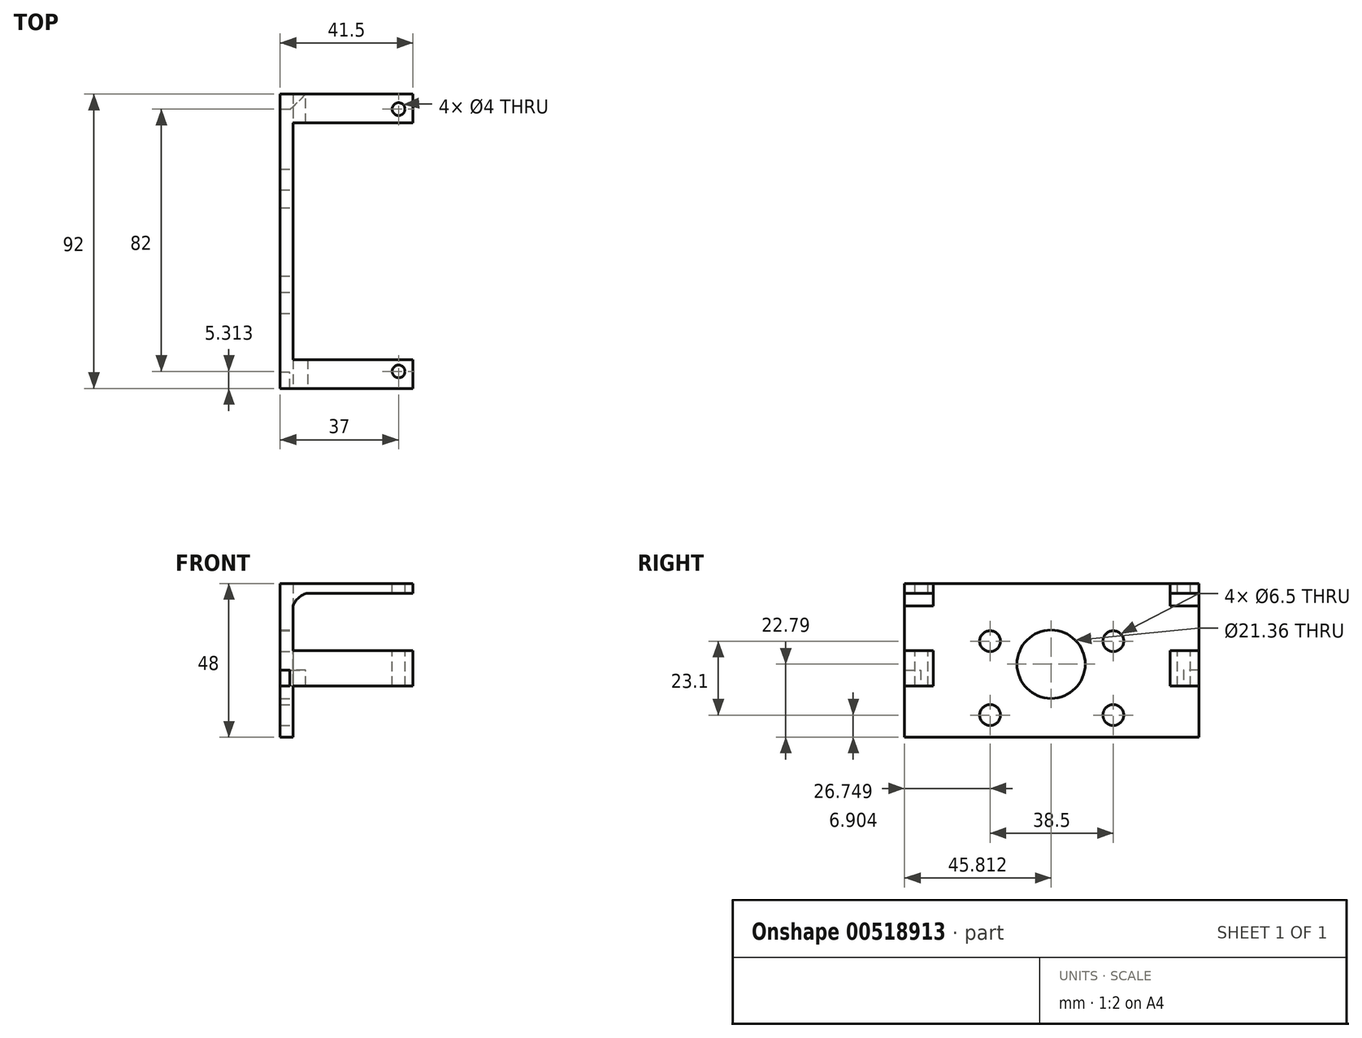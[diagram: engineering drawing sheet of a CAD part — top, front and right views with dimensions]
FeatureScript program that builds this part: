
annotation { "Feature Type Name" : "Feature", "Feature Type Description" : "" }
export const myFeature = defineFeature(function(context is Context, id is Id, definition is map)
    precondition{}
    {
        {
            var Q0;
            Q0=qCreatedBy(makeId("Right.planeOp"),FACE);
            var sketch = newSketch(context, id + "F0", { "sketchPlane" : qUnion([Q0])});
            skLineSegment(sketch, "E0.bottom", {"start": v(-93.03, 7.83) * mm, "end": v(-1.03, 7.83) * mm});
            skLineSegment(sketch, "E0.top", {"start": v(-93.03, -40.17) * mm, "end": v(-1.03, -40.17) * mm});
            skLineSegment(sketch, "E0.left", {"start": v(-93.03, 7.83) * mm, "end": v(-93.03, -40.17) * mm});
            skLineSegment(sketch, "E0.right", {"start": v(-1.03, 7.83) * mm, "end": v(-1.03, -40.17) * mm});
            skSolve(sketch);
        }
        {
            var Q0;
            Q0 = qSketchRegion(id + "F0", true);
            extrude(context, id + "F1", {"entities" : qUnion([Q0]), "depth" : 4 * mm, "offsetDistance" : 25 * mm});
        }
        {
            var Q0;
            Q0=makeQuery(id+"F1.opExtrude","CAP_FACE",FACE,{"disambiguationData":[OSD([sQuery(id+"F0.wireOp",EDGE,"E0.bottom"),sQuery(id+"F0.wireOp",EDGE,"E0.top"),sQuery(id+"F0.wireOp",EDGE,"E0.left"),sQuery(id+"F0.wireOp",EDGE,"E0.right")])],"isStart":false});
            var sketch = newSketch(context, id + "F2", { "sketchPlane" : qUnion([Q0])});
            skCircle(sketch, "E1", {"center": v(-66.28, -10.17) * mm, "radius": 3.25 * mm});
            skCircle(sketch, "E2", {"center": v(-27.78, -10.17) * mm, "radius": 3.25 * mm});
            skCircle(sketch, "E3", {"center": v(-66.28, -33.27) * mm, "radius": 3.25 * mm});
            skCircle(sketch, "E4", {"center": v(-27.78, -33.27) * mm, "radius": 3.25 * mm});
            skLineSegment(sketch, "E5", {"start": v(-27.78, -10.17) * mm, "end": v(-1.03, -10.17) * mm, "construction": true});
            skLineSegment(sketch, "E6", {"start": v(-66.28, -10.17) * mm, "end": v(-93.03, -10.17) * mm, "construction": true});
            skCircle(sketch, "E7", {"center": v(-47.22, -17.38) * mm, "radius": 10.68 * mm});
            skSolve(sketch);
        }
        {
            var Q0;
            Q0 = qSketchRegion(id + "F2", true);
            extrude(context, id + "F3", {"entities" : qUnion([Q0]), "operationType" : NewBodyOperationType.REMOVE, "oppositeDirection" : true, "depth" : 25 * mm, "offsetDistance" : 25 * mm});
        }
        {
            var Q0;
            Q0=makeQuery(id+"F1.opExtrude","CAP_FACE",FACE,{"disambiguationData":[OSD([sQuery(id+"F0.wireOp",EDGE,"E0.bottom"),sQuery(id+"F0.wireOp",EDGE,"E0.top"),sQuery(id+"F0.wireOp",EDGE,"E0.left"),sQuery(id+"F0.wireOp",EDGE,"E0.right")])],"isStart":false});
            var sketch = newSketch(context, id + "F4", { "sketchPlane" : qUnion([Q0])});
            skLineSegment(sketch, "E8.bottom", {"start": v(-93.03, -13.17) * mm, "end": v(-84.03, -13.17) * mm});
            skLineSegment(sketch, "E8.top", {"start": v(-93.03, -24.17) * mm, "end": v(-84.03, -24.17) * mm});
            skLineSegment(sketch, "E8.left", {"start": v(-93.03, -13.17) * mm, "end": v(-93.03, -24.17) * mm});
            skLineSegment(sketch, "E8.right", {"start": v(-84.03, -13.17) * mm, "end": v(-84.03, -24.17) * mm});
            skLineSegment(sketch, "E9.bottom", {"start": v(-1.03, -13.17) * mm, "end": v(-10.03, -13.17) * mm});
            skLineSegment(sketch, "E9.top", {"start": v(-1.03, -24.17) * mm, "end": v(-10.03, -24.17) * mm});
            skLineSegment(sketch, "E9.left", {"start": v(-1.03, -13.17) * mm, "end": v(-1.03, -24.17) * mm});
            skLineSegment(sketch, "E9.right", {"start": v(-10.03, -13.17) * mm, "end": v(-10.03, -24.17) * mm});
            skLineSegment(sketch, "E10.bottom", {"start": v(-93.03, 7.83) * mm, "end": v(-84.03, 7.83) * mm});
            skLineSegment(sketch, "E10.top", {"start": v(-93.03, 4.83) * mm, "end": v(-84.03, 4.83) * mm});
            skLineSegment(sketch, "E10.left", {"start": v(-93.03, 7.83) * mm, "end": v(-93.03, 4.83) * mm});
            skLineSegment(sketch, "E10.right", {"start": v(-84.03, 7.83) * mm, "end": v(-84.03, 4.83) * mm});
            skLineSegment(sketch, "E11.bottom", {"start": v(-1.03, 7.83) * mm, "end": v(-10.03, 7.83) * mm});
            skLineSegment(sketch, "E11.top", {"start": v(-1.03, 4.83) * mm, "end": v(-10.03, 4.83) * mm});
            skLineSegment(sketch, "E11.left", {"start": v(-1.03, 7.83) * mm, "end": v(-1.03, 4.83) * mm});
            skLineSegment(sketch, "E11.right", {"start": v(-10.03, 7.83) * mm, "end": v(-10.03, 4.83) * mm});
            skSolve(sketch);
        }
        {
            var Q0;
            Q0=makeQuery(id+"F4.imprint","IMPRINT",FACE,{"disambiguationData":[TD([[makeQuery(id+"F4.imprint","IMPRINT",EDGE,{"derivedFrom":sQuery(id+"F4.wireOp",EDGE,"E8.bottom")}),-1.0]])]});
            var Q1;
            Q1=makeQuery(id+"F4.imprint","IMPRINT",FACE,{"disambiguationData":[TD([[makeQuery(id+"F4.imprint","IMPRINT",EDGE,{"derivedFrom":sQuery(id+"F4.wireOp",EDGE,"E9.bottom")}),1.0]])]});
            var Q2;
            Q2=makeQuery(id+"F4.imprint","IMPRINT",FACE,{"disambiguationData":[TD([[makeQuery(id+"F4.imprint","IMPRINT",EDGE,{"derivedFrom":sQuery(id+"F4.wireOp",EDGE,"E10.bottom")}),-1.0]])]});
            var Q3;
            Q3=makeQuery(id+"F4.imprint","IMPRINT",FACE,{"disambiguationData":[TD([[makeQuery(id+"F4.imprint","IMPRINT",EDGE,{"derivedFrom":sQuery(id+"F4.wireOp",EDGE,"E11.bottom")}),-1.0]])]});
            extrude(context, id + "F5", {"entities" : qUnion([Q0, Q1, Q2, Q3]), "operationType" : NewBodyOperationType.ADD, "depth" : 37.5 * mm, "offsetDistance" : 25 * mm});
        }
        {
            var Q0;
            Q0=makeQuery(id+"F5.boolean.opBoolean","MERGE",FACE,{"derivedFrom":[makeQuery(id+"F1.opExtrude","SWEPT_FACE",FACE,{"disambiguationData":[OSD([sQuery(id+"F0.wireOp",EDGE,"E0.bottom")])]}),makeQuery(id+"F5.opExtrude","SWEPT_FACE",FACE,{"disambiguationData":[OSD([sQuery(id+"F4.wireOp",EDGE,"E10.bottom")])]}),makeQuery(id+"F5.opExtrude","SWEPT_FACE",FACE,{"disambiguationData":[OSD([sQuery(id+"F4.wireOp",EDGE,"E11.bottom")])]})]});
            var sketch = newSketch(context, id + "F6", { "sketchPlane" : qUnion([Q0])});
            skCircle(sketch, "E12", {"center": v(37, -5.72) * mm, "radius": 2 * mm});
            skCircle(sketch, "E13", {"center": v(37, -87.72) * mm, "radius": 2 * mm});
            skSolve(sketch);
        }
        {
            var Q0;
            Q0 = qSketchRegion(id + "F6", true);
            extrude(context, id + "F7", {"entities" : qUnion([Q0]), "operationType" : NewBodyOperationType.REMOVE, "oppositeDirection" : true, "depth" : 40 * mm, "offsetDistance" : 25 * mm});
        }
        {
            var Q0;
            Q0=makeQuery(id+"F1.opExtrude","CAP_FACE",FACE,{"disambiguationData":[OSD([sQuery(id+"F0.wireOp",EDGE,"E0.bottom"),sQuery(id+"F0.wireOp",EDGE,"E0.top"),sQuery(id+"F0.wireOp",EDGE,"E0.left"),sQuery(id+"F0.wireOp",EDGE,"E0.right")])],"isStart":true});
            var sketch = newSketch(context, id + "F8", { "sketchPlane" : qUnion([Q0])});
            skLineSegment(sketch, "E14.bottom", {"start": v(0.85, -19.22) * mm, "end": v(5.85, -19.22) * mm});
            skLineSegment(sketch, "E14.top", {"start": v(0.85, -24.22) * mm, "end": v(5.85, -24.22) * mm});
            skLineSegment(sketch, "E14.left", {"start": v(0.85, -19.22) * mm, "end": v(0.85, -24.22) * mm});
            skLineSegment(sketch, "E14.right", {"start": v(5.85, -19.22) * mm, "end": v(5.85, -24.22) * mm});
            skLineSegment(sketch, "E15.bottom", {"start": v(93.03, -19.22) * mm, "end": v(88.03, -19.22) * mm});
            skLineSegment(sketch, "E15.top", {"start": v(93.03, -24.22) * mm, "end": v(88.03, -24.22) * mm});
            skLineSegment(sketch, "E15.left", {"start": v(93.03, -19.22) * mm, "end": v(93.03, -24.22) * mm});
            skLineSegment(sketch, "E15.right", {"start": v(88.03, -19.22) * mm, "end": v(88.03, -24.22) * mm});
            skLineSegment(sketch, "E16", {"start": v(27.78, -10.17) * mm, "end": v(5.85, -19.22) * mm, "construction": true});
            skLineSegment(sketch, "E17", {"start": v(5.85, -24.22) * mm, "end": v(27.78, -33.27) * mm, "construction": true});
            skSolve(sketch);
        }
        {
            var Q0;
            Q0=makeQuery(id+"F8.imprint","IMPRINT",FACE,{"disambiguationData":[TD([[makeQuery(id+"F8.imprint","IMPRINT",EDGE,{"derivedFrom":sQuery(id+"F8.wireOp",EDGE,"E14.bottom")}),-1.0]])]});
            var Q1;
            Q1=makeQuery(id+"F8.imprint","IMPRINT",FACE,{"disambiguationData":[TD([[makeQuery(id+"F8.imprint","IMPRINT",EDGE,{"derivedFrom":sQuery(id+"F8.wireOp",EDGE,"E15.bottom")}),1.0]])]});
            extrude(context, id + "F9", {"entities" : qUnion([Q0, Q1]), "operationType" : NewBodyOperationType.REMOVE, "oppositeDirection" : true, "depth" : 3 * mm, "offsetDistance" : 25 * mm});
        }
        {
            var Q0;
            Q0=makeQuery(id+"F9.boolean.opBoolean","INTERSECT",EDGE,{"derivedFrom":[makeQuery(id+"F5.boolean.opBoolean","MERGE",FACE,{"derivedFrom":[makeQuery(id+"F1.opExtrude","SWEPT_FACE",FACE,{"disambiguationData":[OSD([sQuery(id+"F0.wireOp",EDGE,"E0.right")])]}),makeQuery(id+"F5.opExtrude","SWEPT_FACE",FACE,{"disambiguationData":[OSD([sQuery(id+"F4.wireOp",EDGE,"E9.left")])]}),makeQuery(id+"F5.opExtrude","SWEPT_FACE",FACE,{"disambiguationData":[OSD([sQuery(id+"F4.wireOp",EDGE,"E11.left")])]})]}),makeQuery(id+"F9.opExtrude","CAP_FACE",FACE,{"disambiguationData":[OSD([sQuery(id+"F8.wireOp",EDGE,"E14.bottom"),sQuery(id+"F8.wireOp",EDGE,"E14.top"),sQuery(id+"F8.wireOp",EDGE,"E14.left"),sQuery(id+"F8.wireOp",EDGE,"E14.right")])],"isStart":false})]});
            chamfer(context, id + "F10", {"entities" : qUnion([Q0]), "width" : 5 * mm, "tangentPropagation" : true});
        }
        {
            var Q0;
            Q0=makeQuery(id+"F5.boolean.opBoolean","MERGE",FACE,{"derivedFrom":[makeQuery(id+"F1.opExtrude","SWEPT_FACE",FACE,{"disambiguationData":[OSD([sQuery(id+"F0.wireOp",EDGE,"E0.right")])]}),makeQuery(id+"F5.opExtrude","SWEPT_FACE",FACE,{"disambiguationData":[OSD([sQuery(id+"F4.wireOp",EDGE,"E9.left")])]}),makeQuery(id+"F5.opExtrude","SWEPT_FACE",FACE,{"disambiguationData":[OSD([sQuery(id+"F4.wireOp",EDGE,"E11.left")])]})]});
            var sketch = newSketch(context, id + "F11", { "sketchPlane" : qUnion([Q0])});
            skArc(sketch, "E18", {"start": v(-4, 0.83) * mm, "mid": v(-5.54, 3.3) * mm, "end": v(-8, 4.83) * mm});
            skLineSegment(sketch, "E19", {"start": v(-8, 4.83) * mm, "end": v(-4, 4.83) * mm});
            skLineSegment(sketch, "E20", {"start": v(-4, 4.83) * mm, "end": v(-4, 0.83) * mm});
            skLineSegment(sketch, "E21", {"start": v(-8.03, 7.83) * mm, "end": v(0, 14.63) * mm});
            skLineSegment(sketch, "E22", {"start": v(0, 14.63) * mm, "end": v(0, 7.83) * mm});
            skLineSegment(sketch, "E23", {"start": v(0, 7.83) * mm, "end": v(-8.07, 7.88) * mm});
            skSolve(sketch);
        }
        {
            var Q0;
            Q0=makeQuery(id+"F11.imprint","IMPRINT",FACE,{"disambiguationData":[TD([[makeQuery(id+"F11.imprint","IMPRINT",EDGE,{"derivedFrom":sQuery(id+"F11.wireOp",EDGE,"E18")}),-1.0]])]});
            extrude(context, id + "F12", {"entities" : qUnion([Q0]), "operationType" : NewBodyOperationType.ADD, "oppositeDirection" : true, "depth" : 9 * mm, "offsetDistance" : 25 * mm});
        }
        {
            var Q0;
            Q0=makeQuery(id+"F5.boolean.opBoolean","MERGE",FACE,{"derivedFrom":[makeQuery(id+"F1.opExtrude","SWEPT_FACE",FACE,{"disambiguationData":[OSD([sQuery(id+"F0.wireOp",EDGE,"E0.left")])]}),makeQuery(id+"F5.opExtrude","SWEPT_FACE",FACE,{"disambiguationData":[OSD([sQuery(id+"F4.wireOp",EDGE,"E8.left")])]}),makeQuery(id+"F5.opExtrude","SWEPT_FACE",FACE,{"disambiguationData":[OSD([sQuery(id+"F4.wireOp",EDGE,"E10.left")])]})]});
            var sketch = newSketch(context, id + "F13", { "sketchPlane" : qUnion([Q0])});
            skArc(sketch, "E24", {"start": v(8.52, 4.83) * mm, "mid": v(5.75, 3.4) * mm, "end": v(4, 0.83) * mm});
            skLineSegment(sketch, "E25", {"start": v(8.52, 4.83) * mm, "end": v(4, 4.83) * mm});
            skLineSegment(sketch, "E26", {"start": v(4, 4.83) * mm, "end": v(4, 0.83) * mm});
            skSolve(sketch);
        }
        {
            var Q0;
            Q0=makeQuery(id+"F13.imprint","IMPRINT",FACE,{"disambiguationData":[TD([[makeQuery(id+"F13.imprint","IMPRINT",EDGE,{"derivedFrom":sQuery(id+"F13.wireOp",EDGE,"E24")}),-1.0]])]});
            extrude(context, id + "F14", {"entities" : qUnion([Q0]), "operationType" : NewBodyOperationType.ADD, "oppositeDirection" : true, "depth" : 9 * mm, "offsetDistance" : 25 * mm});
        }
    });
